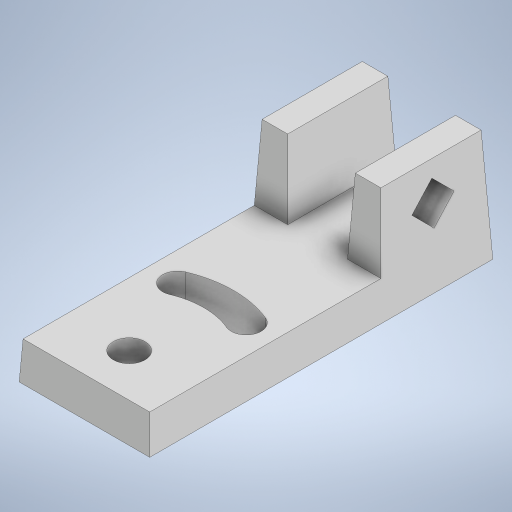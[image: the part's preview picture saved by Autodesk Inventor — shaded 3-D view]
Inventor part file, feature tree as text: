
AUTODESK INVENTOR PART (.ipt)
format: ipt  version: 2023 (Build 270158000, 158)  size: 287,744 bytes
history: native  units: mm
features: other x4, extrude x3, sketch x2
ambient origin geometry x8: Origin, YZ Plane, XZ Plane, XY Plane, X Axis, Y Axis, Z Axis, Center Point
bodies: Solido1 (feature_tree)
feature tree (9):
  sketch  "Schizzo1"
  extrude  "Estrusione1"  Depth=12.0mm
  extrude  "Estrusione2"  Depth=8.5mm
  other  "Sformo faccia1"
  other  "Sformo faccia2"
  extrude  "Estrusione3"  Depth=82.0mm
  sketch  "Schizzo2"
  other  "Linea chiusa proiettata1"
  other  "Linea chiusa proiettata2"
